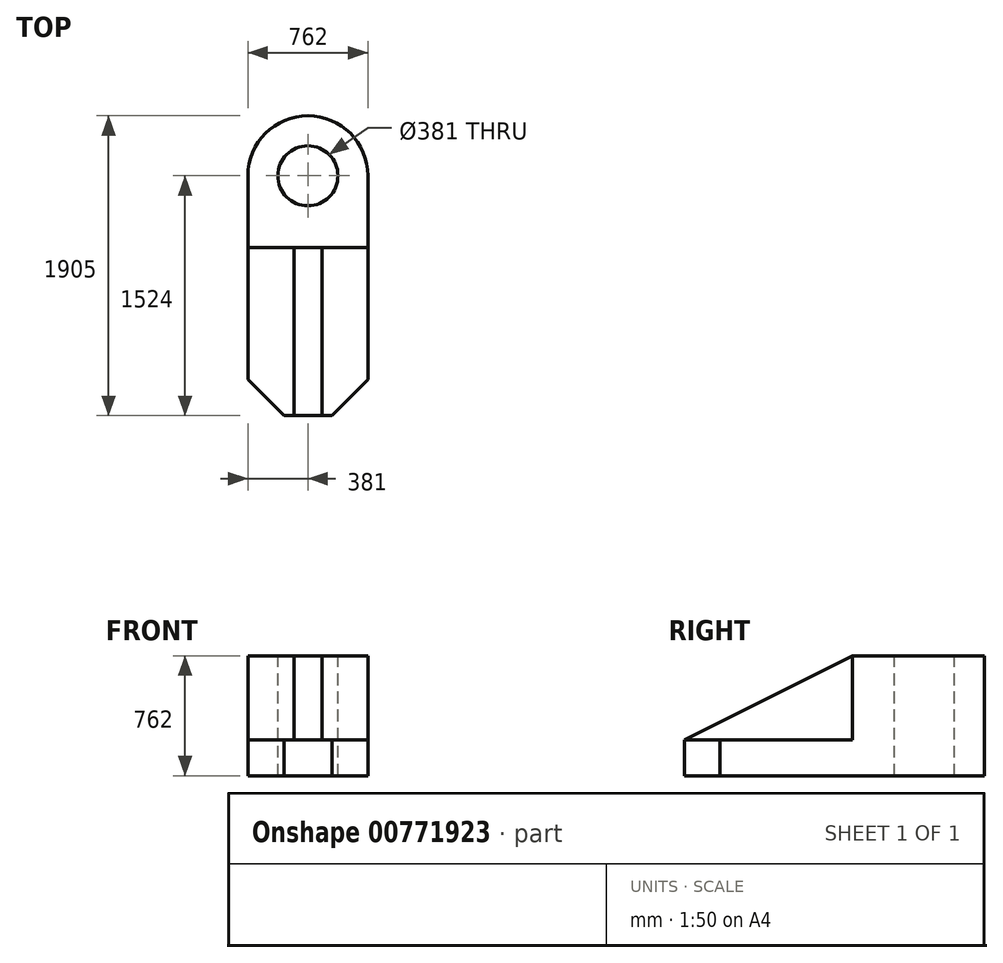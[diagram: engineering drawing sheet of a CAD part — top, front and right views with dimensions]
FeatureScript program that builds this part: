
annotation { "Feature Type Name" : "Feature", "Feature Type Description" : "" }
export const myFeature = defineFeature(function(context is Context, id is Id, definition is map)
    precondition{}
    {
        {
            var Q0;
            Q0=qCreatedBy(makeId("Top.planeOp"),FACE);
            var sketch = newSketch(context, id + "F0", { "sketchPlane" : qUnion([Q0])});
            skLineSegment(sketch, "E0", {"start": v(0, 0) * mm, "end": v(0, 2061.05) * mm, "construction": true});
            skLineSegment(sketch, "E1", {"start": v(0, 0) * mm, "end": v(-381, 0) * mm});
            skLineSegment(sketch, "E2", {"start": v(-381, 0) * mm, "end": v(-381, 1524) * mm});
            skLineSegment(sketch, "E3", {"start": v(0, 1905) * mm, "end": v(0, 1905) * mm});
            skPoint(sketch, "E4.start.orphan", {"position": v(388.93, 0) * mm});
            skPoint(sketch, "E5.visualSharp", {"position": v(-381, 1905) * mm});
            skArc(sketch, "E5.filletArc", {"start": v(0, 1905) * mm, "mid": v(-269.4, 1793.4) * mm, "end": v(-381, 1524) * mm});
            skLineSegment(sketch, "E6.MirrorCS", {"start": v(0, 0) * mm, "end": v(381, 0) * mm});
            skLineSegment(sketch, "E7.MirrorCS", {"start": v(381, 0) * mm, "end": v(381, 1524) * mm});
            skArc(sketch, "E8.MirrorCS", {"start": v(0, 1905) * mm, "mid": v(269.4, 1793.4) * mm, "end": v(381, 1524) * mm});
            skCircle(sketch, "E9", {"center": v(0, 1524) * mm, "radius": 190.5 * mm});
            skSolve(sketch);
        }
        {
            var Q0;
            Q0 = qSketchRegion(id + "F0", true);
            extrude(context, id + "F1", {"entities" : qUnion([Q0]), "oppositeDirection" : true, "depth" : 228.6 * mm, "offsetDistance" : 25.4 * mm});
        }
        {
            var Q0;
            Q0=makeQuery(id+"F1.opExtrude","CAP_FACE",FACE,{"disambiguationData":[OSD([sQuery(id+"F0.wireOp",EDGE,"E1"),sQuery(id+"F0.wireOp",EDGE,"E2"),sQuery(id+"F0.wireOp",EDGE,"E5.filletArc"),sQuery(id+"F0.wireOp",EDGE,"E6.MirrorCS"),sQuery(id+"F0.wireOp",EDGE,"E7.MirrorCS"),sQuery(id+"F0.wireOp",EDGE,"E8.MirrorCS")])],"isStart":true});
            var sketch = newSketch(context, id + "F2", { "sketchPlane" : qUnion([Q0])});
            skCircle(sketch, "E10", {"center": v(0, 1524) * mm, "radius": 190.5 * mm});
            skCircle(sketch, "E11", {"center": v(0, 1524) * mm, "radius": 381 * mm});
            skLineSegment(sketch, "E12", {"start": v(-381, 1524) * mm, "end": v(-381, 1066.8) * mm});
            skLineSegment(sketch, "E13", {"start": v(-381, 1066.8) * mm, "end": v(381, 1066.8) * mm});
            skLineSegment(sketch, "E14", {"start": v(381, 1066.8) * mm, "end": v(381, 1524) * mm});
            skSolve(sketch);
        }
        {
            var Q0;
            Q0 = qSketchRegion(id + "F2", true);
            extrude(context, id + "F3", {"entities" : qUnion([Q0]), "operationType" : NewBodyOperationType.ADD, "depth" : 533.4 * mm, "offsetDistance" : 25.4 * mm});
        }
        {
            var Q0;
            Q0=qCreatedBy(makeId("Right.planeOp"),FACE);
            var sketch = newSketch(context, id + "F4", { "sketchPlane" : qUnion([Q0])});
            skLineSegment(sketch, "E15", {"start": v(0, 0) * mm, "end": v(1066.8, 533.4) * mm});
            skLineSegment(sketch, "E16", {"start": v(1066.8, 533.4) * mm, "end": v(1066.8, 0) * mm});
            skLineSegment(sketch, "E17", {"start": v(1066.8, 0) * mm, "end": v(0, 0) * mm});
            skSolve(sketch);
        }
        {
            var Q0;
            Q0 = qSketchRegion(id + "F4", true);
            extrude(context, id + "F5", {"entities" : qUnion([Q0]), "operationType" : NewBodyOperationType.ADD, "depth" : 177.8 * mm, "offsetDistance" : 25.4 * mm, "symmetric" : true});
        }
        {
            var Q0;
            Q0=makeQuery(id+"F1.opExtrude","SWEPT_EDGE",EDGE,{"disambiguationData":[OSD([sQuery(id+"F0.wireOp",EDGE,"E1"),sQuery(id+"F0.wireOp",EDGE,"E2")])]});
            chamfer(context, id + "F6", {"entities" : qUnion([Q0]), "width" : 228.6 * mm, "tangentPropagation" : true});
        }
        {
            var Q0;
            Q0=makeQuery(id+"F1.opExtrude","SWEPT_EDGE",EDGE,{"disambiguationData":[OSD([sQuery(id+"F0.wireOp",EDGE,"E6.MirrorCS"),sQuery(id+"F0.wireOp",EDGE,"E7.MirrorCS")])]});
            chamfer(context, id + "F7", {"entities" : qUnion([Q0]), "width" : 228.6 * mm, "tangentPropagation" : true});
        }
    });
